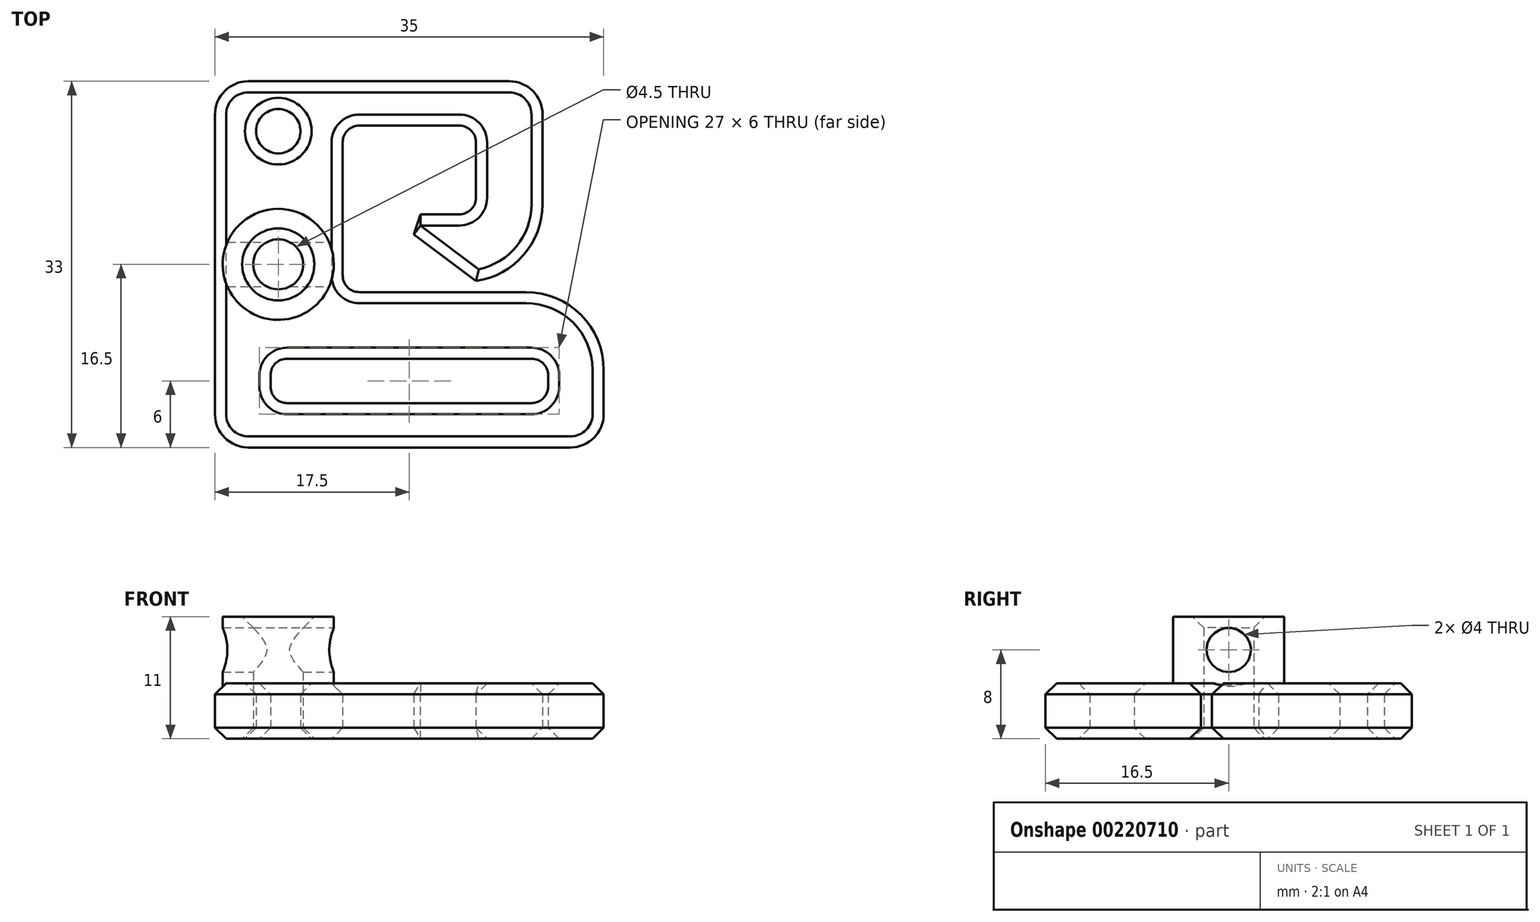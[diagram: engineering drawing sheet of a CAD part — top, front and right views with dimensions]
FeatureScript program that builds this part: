
annotation { "Feature Type Name" : "Feature", "Feature Type Description" : "" }
export const myFeature = defineFeature(function(context is Context, id is Id, definition is map)
    precondition{}
    {
        {
            var Q0;
            Q0=qCreatedBy(makeId("Top.planeOp"),FACE);
            var sketch = newSketch(context, id + "F0", { "sketchPlane" : qUnion([Q0])});
            skLineSegment(sketch, "E0.bottom", {"start": v(12.5, 2) * mm, "end": v(-12.5, 2) * mm});
            skLineSegment(sketch, "E0.top", {"start": v(12.5, -2) * mm, "end": v(-12.5, -2) * mm});
            skLineSegment(sketch, "E0.left", {"start": v(12.5, 2) * mm, "end": v(12.5, -2) * mm});
            skLineSegment(sketch, "E0.right", {"start": v(-12.5, 2) * mm, "end": v(-12.5, -2) * mm});
            skPoint(sketch, "E0.middle", {"position": v(0, 0) * mm});
            skLineSegment(sketch, "E1.bottom", {"start": v(6, 23) * mm, "end": v(-6, 23) * mm});
            skLineSegment(sketch, "E1.top", {"start": v(17.5, 8) * mm, "end": v(-6, 8) * mm});
            skLineSegment(sketch, "E1.left", {"start": v(6, 23) * mm, "end": v(6, 8) * mm});
            skLineSegment(sketch, "E1.right", {"start": v(-6, 23) * mm, "end": v(-6, 8) * mm});
            skPoint(sketch, "E1.middle", {"position": v(0, 15.5) * mm});
            skLineSegment(sketch, "E2.bottom", {"start": v(-17.5, 27) * mm, "end": v(17.5, 27) * mm});
            skLineSegment(sketch, "E2.top", {"start": v(-17.5, -6) * mm, "end": v(17.5, -6) * mm});
            skLineSegment(sketch, "E2.left", {"start": v(-17.5, 27) * mm, "end": v(-17.5, -6) * mm});
            skLineSegment(sketch, "E2.right", {"start": v(17.5, 27) * mm, "end": v(17.5, -6) * mm});
            skPoint(sketch, "E2.middle", {"position": v(0, 10.5) * mm});
            skPoint(sketch, "E2.middle.positionSnap0", {"position": v(0, 23) * mm});
            skPoint(sketch, "E2.centerSnap0", {"position": v(0, 23) * mm});
            skLineSegment(sketch, "E3", {"start": v(17.5, 9) * mm, "end": v(6, 9) * mm});
            skCircle(sketch, "E4", {"center": v(-11.8, 10.5) * mm, "radius": 5 * mm});
            skLineSegment(sketch, "E5", {"start": v(12, 27) * mm, "end": v(12, 9) * mm});
            skCircle(sketch, "E6", {"center": v(-11.8, 22.5) * mm, "radius": 2 * mm});
            skLineSegment(sketch, "E7", {"start": v(6, 15) * mm, "end": v(-2, 15) * mm});
            skLineSegment(sketch, "E8", {"start": v(-2, 15) * mm, "end": v(6, 9) * mm});
            skPoint(sketch, "E9", {"position": v(6, 15.5) * mm});
            skCircle(sketch, "E10", {"center": v(-11.8, 10.5) * mm, "radius": 2.25 * mm});
            skSolve(sketch);
        }
        {
            var Q0;
            Q0=qCreatedBy(makeId("Right.planeOp"),FACE);
            var sketch = newSketch(context, id + "F1", { "sketchPlane" : qUnion([Q0])});
            skCircle(sketch, "E11", {"center": v(10.5, 8) * mm, "radius": 2 * mm});
            skSolve(sketch);
        }
        {
            var Q0;
            Q0=makeQuery(id+"F0.imprint","IMPRINT",FACE,{"disambiguationData":[TD([[makeQuery(id+"F0.imprint","IMPRINT",EDGE,{"derivedFrom":sQuery(id+"F0.wireOp",EDGE,"E0.bottom")}),-1.0]])]});
            var Q1;
            {var subQ0=sQuery(id+"F0.wireOp",EDGE,"rsBg8Wjm-E8yl-bHjy-INXi-T6D7uWffA7Lq");Q1=makeQuery(id+"F0.imprint","IMPRINT",FACE,{"disambiguationData":[TD([[makeQuery(id+"F0.imprint","IMPRINT",EDGE,{"derivedFrom":subQ0}),-1.0]])]});}
            var Q2;
            {var subQ0=sQuery(id+"F0.wireOp",EDGE,"E7");Q2=makeQuery(id+"F0.imprint","IMPRINT",FACE,{"disambiguationData":[TD([[makeQuery(id+"F0.imprint","IMPRINT",EDGE,{"derivedFrom":subQ0}),1.0]])]});}
            extrude(context, id + "F2", {"entities" : qUnion([Q0, Q1, Q2]), "depth" : 5 * mm});
        }
        {
            var Q0;
            Q0=makeQuery(id+"F0.imprint","IMPRINT",FACE,{"disambiguationData":[TD([[makeQuery(id+"F0.imprint","IMPRINT",EDGE,{"derivedFrom":sQuery(id+"F0.wireOp",EDGE,"E4")}),1.0]])]});
            extrude(context, id + "F3", {"entities" : qUnion([Q0]), "operationType" : NewBodyOperationType.ADD, "depth" : 11 * mm});
        }
        {
            var Q0;
            Q0 = qSketchRegion(id + "F1", true);
            var Q1;
            Q1=sQuery(id+"F1.wireOp",EDGE,"E11");
            var Q2;
            Q2=makeQuery(id+"F2.opExtrude","SWEPT_BODY",BODY,{"disambiguationData":[OSD([sQuery(id+"F0.wireOp",EDGE,"E0.bottom"),sQuery(id+"F0.wireOp",EDGE,"E0.top"),sQuery(id+"F0.wireOp",EDGE,"E0.left"),sQuery(id+"F0.wireOp",EDGE,"E0.right"),sQuery(id+"F0.wireOp",EDGE,"E1.bottom"),sQuery(id+"F0.wireOp",EDGE,"E1.top"),sQuery(id+"F0.wireOp",EDGE,"E1.left"),sQuery(id+"F0.wireOp",EDGE,"E1.right"),sQuery(id+"F0.wireOp",EDGE,"E2.bottom"),sQuery(id+"F0.wireOp",EDGE,"E2.top"),sQuery(id+"F0.wireOp",EDGE,"E2.left"),sQuery(id+"F0.wireOp",EDGE,"E2.right"),sQuery(id+"F0.wireOp",EDGE,"E3"),sQuery(id+"F0.wireOp",EDGE,"rsBg8Wjm-E8yl-bHjy-INXi-T6D7uWffA7Lq"),sQuery(id+"F0.wireOp",EDGE,"E4")])]});
            extrude(context, id + "F4", {"entities" : qUnion([Q0]), "operationType" : NewBodyOperationType.REMOVE, "surfaceEntities" : qUnion([Q1]), "endBound" : BoundingType.THROUGH_ALL, "oppositeDirection" : true, "endBoundEntityBody" : qUnion([Q2]), "depth" : 25 * mm});
        }
        {
            var Q0;
            Q0=makeQuery(id+"F2.opExtrude","SWEPT_EDGE",EDGE,{"disambiguationData":[OSD([sQuery(id+"F0.wireOp",EDGE,"E2.bottom"),sQuery(id+"F0.wireOp",EDGE,"E5")])]});
            var Q1;
            Q1=makeQuery(id+"F2.opExtrude","SWEPT_EDGE",EDGE,{"disambiguationData":[OSD([sQuery(id+"F0.wireOp",EDGE,"E2.top"),sQuery(id+"F0.wireOp",EDGE,"E2.left")])]});
            var Q2;
            Q2=makeQuery(id+"F2.opExtrude","SWEPT_EDGE",EDGE,{"disambiguationData":[OSD([sQuery(id+"F0.wireOp",EDGE,"E2.top"),sQuery(id+"F0.wireOp",EDGE,"E2.right")])]});
            var Q3;
            Q3=makeQuery(id+"F2.opExtrude","CAP_EDGE",EDGE,{"disambiguationData":[OSD([sQuery(id+"F0.wireOp",EDGE,"E4")])],"isStart":false});
            var Q4;
            Q4=makeQuery(id+"F2.opExtrude","SWEPT_EDGE",EDGE,{"disambiguationData":[OSD([sQuery(id+"F0.wireOp",EDGE,"E2.bottom"),sQuery(id+"F0.wireOp",EDGE,"E2.left")])]});
            fillet(context, id + "F5", {"entities" : qUnion([Q0, Q1, Q2, Q3, Q4]), "radius" : 3 * mm, "tangentPropagation" : true, "allowEdgeOverflow" : false});
        }
        {
            var Q0;
            Q0=makeQuery(id+"F2.opExtrude","SWEPT_EDGE",EDGE,{"disambiguationData":[OSD([sQuery(id+"F0.wireOp",EDGE,"E1.bottom"),sQuery(id+"F0.wireOp",EDGE,"E1.left")])]});
            var Q1;
            Q1=makeQuery(id+"F2.opExtrude","SWEPT_EDGE",EDGE,{"disambiguationData":[OSD([sQuery(id+"F0.wireOp",EDGE,"E1.top"),sQuery(id+"F0.wireOp",EDGE,"E1.right")])]});
            var Q2;
            Q2=makeQuery(id+"F2.opExtrude","SWEPT_EDGE",EDGE,{"disambiguationData":[OSD([sQuery(id+"F0.wireOp",EDGE,"E1.left"),sQuery(id+"F0.wireOp",EDGE,"rsBg8Wjm-E8yl-bHjy-INXi-T6D7uWffA7Lq")])]});
            var Q3;
            Q3=makeQuery(id+"F2.opExtrude","SWEPT_EDGE",EDGE,{"disambiguationData":[OSD([sQuery(id+"F0.wireOp",EDGE,"E1.top"),sQuery(id+"F0.wireOp",EDGE,"E1.right")])]});
            var Q4;
            Q4=makeQuery(id+"F2.opExtrude","SWEPT_EDGE",EDGE,{"disambiguationData":[OSD([sQuery(id+"F0.wireOp",EDGE,"E1.bottom"),sQuery(id+"F0.wireOp",EDGE,"E1.left")])]});
            var Q5;
            Q5=makeQuery(id+"F2.opExtrude","SWEPT_EDGE",EDGE,{"disambiguationData":[OSD([sQuery(id+"F0.wireOp",EDGE,"E1.bottom"),sQuery(id+"F0.wireOp",EDGE,"E1.right")])]});
            var Q6;
            Q6=makeQuery(id+"F2.opExtrude","SWEPT_EDGE",EDGE,{"disambiguationData":[OSD([sQuery(id+"F0.wireOp",EDGE,"E0.top"),sQuery(id+"F0.wireOp",EDGE,"E0.left")])]});
            var Q7;
            Q7=makeQuery(id+"F2.opExtrude","SWEPT_EDGE",EDGE,{"disambiguationData":[OSD([sQuery(id+"F0.wireOp",EDGE,"E0.top"),sQuery(id+"F0.wireOp",EDGE,"E0.right")])]});
            var Q8;
            Q8=makeQuery(id+"F2.opExtrude","SWEPT_EDGE",EDGE,{"disambiguationData":[OSD([sQuery(id+"F0.wireOp",EDGE,"E0.bottom"),sQuery(id+"F0.wireOp",EDGE,"E0.left")])]});
            var Q9;
            Q9=makeQuery(id+"F2.opExtrude","SWEPT_EDGE",EDGE,{"disambiguationData":[OSD([sQuery(id+"F0.wireOp",EDGE,"E0.bottom"),sQuery(id+"F0.wireOp",EDGE,"E0.right")])]});
            fillet(context, id + "F6", {"entities" : qUnion([Q0, Q1, Q2, Q3, Q4, Q5, Q6, Q7, Q8, Q9]), "radius" : 1.5 * mm, "tangentPropagation" : true, "allowEdgeOverflow" : false});
        }
        {
            var Q0;
            Q0=makeQuery(id+"F2.opExtrude","SWEPT_EDGE",EDGE,{"disambiguationData":[OSD([sQuery(id+"F0.wireOp",EDGE,"E3"),sQuery(id+"F0.wireOp",EDGE,"E5")])]});
            var Q1;
            Q1=makeQuery(id+"F2.opExtrude","SWEPT_EDGE",EDGE,{"disambiguationData":[OSD([sQuery(id+"F0.wireOp",EDGE,"E1.top"),sQuery(id+"F0.wireOp",EDGE,"E2.right")])]});
            fillet(context, id + "F7", {"entities" : qUnion([Q0, Q1]), "radius" : 7 * mm, "tangentPropagation" : true, "allowEdgeOverflow" : false});
        }
        {
            var Q0;
            Q0=makeQuery(id+"F2.opExtrude","CAP_EDGE",EDGE,{"disambiguationData":[OSD([sQuery(id+"F0.wireOp",EDGE,"E0.top")])],"isStart":false});
            var Q1;
            Q1=makeQuery(id+"F2.opExtrude","CAP_EDGE",EDGE,{"disambiguationData":[OSD([sQuery(id+"F0.wireOp",EDGE,"E0.top")])],"isStart":true});
            var Q2;
            Q2=makeQuery(id+"F2.opExtrude","CAP_EDGE",EDGE,{"disambiguationData":[OSD([sQuery(id+"F0.wireOp",EDGE,"E2.top")])],"isStart":false});
            var Q3;
            Q3=makeQuery(id+"F2.opExtrude","CAP_EDGE",EDGE,{"disambiguationData":[OSD([sQuery(id+"F0.wireOp",EDGE,"E2.top")])],"isStart":true});
            var Q4;
            Q4=makeQuery(id+"F2.opExtrude","CAP_EDGE",EDGE,{"disambiguationData":[OSD([sQuery(id+"F0.wireOp",EDGE,"E1.left")])],"isStart":false});
            var Q5;
            Q5=makeQuery(id+"F2.opExtrude","CAP_EDGE",EDGE,{"disambiguationData":[OSD([sQuery(id+"F0.wireOp",EDGE,"E6")])],"isStart":false});
            var Q6;
            Q6=makeQuery(id+"F2.opExtrude","CAP_EDGE",EDGE,{"disambiguationData":[OSD([sQuery(id+"F0.wireOp",EDGE,"E6")])],"isStart":true});
            var Q7;
            Q7=makeQuery(id+"F2.opExtrude","CAP_EDGE",EDGE,{"disambiguationData":[OSD([sQuery(id+"F0.wireOp",EDGE,"E8")])],"isStart":false});
            var Q8;
            Q8=makeQuery(id+"F2.opExtrude","CAP_EDGE",EDGE,{"disambiguationData":[OSD([sQuery(id+"F0.wireOp",EDGE,"E8")])],"isStart":true});
            var Q9;
            Q9=makeQuery(id+"F2.opExtrude","SWEPT_EDGE",EDGE,{"disambiguationData":[OSD([sQuery(id+"F0.wireOp",EDGE,"E7"),sQuery(id+"F0.wireOp",EDGE,"E8")])]});
            var Q10;
            Q10=makeQuery(id+"F3.opExtrude","CAP_EDGE",EDGE,{"disambiguationData":[OSD([sQuery(id+"F0.wireOp",EDGE,"E10")])],"isStart":true});
            var Q11;
            Q11=makeQuery(id+"F3.opExtrude","CAP_EDGE",EDGE,{"disambiguationData":[OSD([sQuery(id+"F0.wireOp",EDGE,"E10")])],"isStart":false});
            chamfer(context, id + "F8", {"entities" : qUnion([Q0, Q1, Q2, Q3, Q4, Q5, Q6, Q7, Q8, Q9, Q10, Q11]), "width" : 1 * mm, "tangentPropagation" : true});
        }
    });
